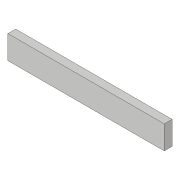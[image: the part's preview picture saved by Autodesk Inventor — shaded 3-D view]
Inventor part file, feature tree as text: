
AUTODESK INVENTOR PART (.ipt)
format: ipt  version: 2018 (Build 220112000, 112)  size: 73,216 bytes
history: native  units: in
note: dims shown in document units (in); Inventor stores cm internally (conversion verified against a paired STEP export)
features: extrude x1, sketch x1
ambient origin geometry x8: Origin, YZ Plane, XZ Plane, XY Plane, X Axis, Y Axis, Z Axis, Center Point
bodies: Solid1 (feature_tree)
feature tree (2):
  extrude  "Extrusion1"  Depth=3.937in
  sketch  "Sketch1"  dims[d0=0.5906in d1=3.937in d2=0.5906in d3=0.1969in d4=0.0in]
